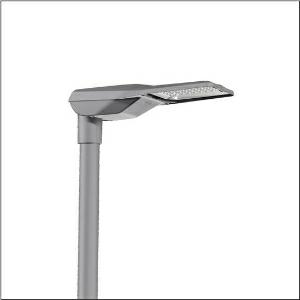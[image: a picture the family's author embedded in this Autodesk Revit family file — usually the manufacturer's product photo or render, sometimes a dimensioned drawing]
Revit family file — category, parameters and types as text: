
# Revit family: streetlight_sl_21_iq_mini___st0_8a_5xe2c31g08gb_0650
name_source: partatom
category: Lighting Fixtures
units: mm (PartAtom-declared; Revit-internal decimal feet)

## family parameters
Cut with Voids When Loaded = No
Host = Face
Light Source = No
Part Type = Normal
Room Calculation Point = No
Round Connector Dimension = Use Diameter
Shared = No

## types (1)
- --- (1 x LED, 5680 lm, 37.1 W, 3000K)
    Apparent Load = 37 VA
    CIE Flux Codes = 38 75 97 100 100
    Color Rendering = 70
    Color Temperature = 3000K
    Default Elevation = 1800 mm
    Description = Streetlight SL 21 iQ mini, mast luminaire, primary light control with lens, of PMMA, primary optical cover: cover, of toughened safety glass, transparent, light distribution: ST0.8a, light emission: direct distribution, primary light characteristic: asymmetric, installation type: post-top, side-entry, LED, High Power LED, rated luminous flux: 5.680lm, luminous efficacy: 153lm/W, light colour: 730, colour temperature: 3000K, control gear: iQ Street-Remote, control: Street-Remote, Auto-Match, Temp-Guard, Lumen-Switch, Night-Set, Smart-Wire, Light-Fading, Desk-Remote (wireless, voltage-free reading and setting of iQ features in the workshop via application-optimized NFC function/RFID function), optimised constant luminous flux control (CLO 2.0), pre-setting: linear dimming characteristic, mains connection: 220..240V, AC, 50/60Hz, start of lifetime: 37W, end of service life: 39W, reduction: 18W, luminaire housing, of diecast aluminium, powder-coated, SITECO metallic grey (DB 702S), corrosivity category C5 high according to DIN EN ISO 12944, please order mast flange separately, inclination adjustable: 0°, 5°, 10°, 15°, sealing non-destructively replaceable, multi-level sealing system, length: 628mm, width: 235mm, height: 110mm, mast flange for spigot size: 42mm (side-entry): 5XC10008XM4, 60/48mm (side-entry/post-top): 5XC10108XM2, 76/60mm (side-entry/post-top): 5XC10108XM1, mounting height: 4..8m, protection rating (complete): IP66, insulation class (complete): insulation class II (safety insulation), certification: CE, ENEC, ENEC+, VDE, impact resistance: IK10, permissible operating ambient temperature for outdoor applications: -40..+50°C, standard-compliant lighting for roads and squares, packaging unit: 1 piece

Light Distribution: ST0.8a
    Height = 110 mm
    Lamp = 1 x LED
    Lamp Light Flux = 5680 lm
    Lamp Power = 37.1 W
    Lamp count = 1
    Length = 625 mm
    Luminous efficacy = 153 lm/W
    Manufacturer = Siteco
    ModVariant = No
    Model = 5XE2C31G08GB
    Number of Poles = 1
    OnlyDefault = Yes
    Power Factor = 1
    Product Name = Streetlight SL 21 iQ mini | ST0.8a
    Product group = mast luminaire | pylon top
    ProductGroupID = 6100
    Protection Class = Protection class II
    Protection Degree = IP 66
    RLX_Detail_Level = 1
    RLX_Emergency_Light_Flux = 0 lm
    RLX_Emergency_Type = 0
    RLX_Emergency_Type_DB = No
    RlxData = <blob elided: 26349 chars, md5=893a87b6>
    Socket = socket
    Standby Power = 0 W
    System Light Flux = 5680 lm
    System Power = 37 W
    Type Comments = factory setting: luminous flux: 100 % | dim-lin: 254 | 385 mA
    Type Image = l_1003519.jpg
    URL = http://relux.com
    VarID = @adj_183143
    Voltage = 0 V
    Weight = 0.00 kg
    Width = 234 mm

## geometry (parser evidence)
native form markers: Blend x4, Sweep x9
no freeform markers — native parametric forms only
